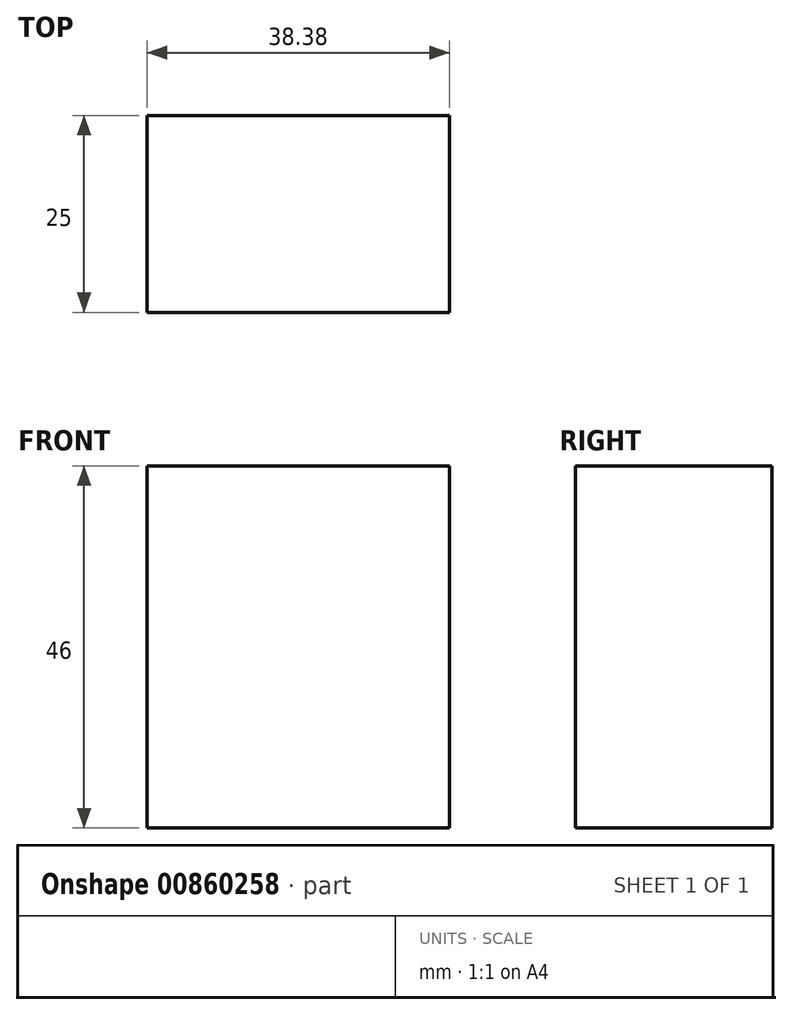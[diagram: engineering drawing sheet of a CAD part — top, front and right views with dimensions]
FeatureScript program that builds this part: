
annotation { "Feature Type Name" : "Feature", "Feature Type Description" : "" }
export const myFeature = defineFeature(function(context is Context, id is Id, definition is map)
    precondition{}
    {
        {
            var Q0;
            Q0=qCreatedBy(makeId("Front.planeOp"),FACE);
            var sketch = newSketch(context, id + "F0", { "sketchPlane" : qUnion([Q0])});
            skLineSegment(sketch, "E0.bottom", {"start": v(-116.32, 40.69) * mm, "end": v(-77.94, 40.69) * mm});
            skLineSegment(sketch, "E0.top", {"start": v(-116.32, -5.3) * mm, "end": v(-77.94, -5.3) * mm});
            skLineSegment(sketch, "E0.left", {"start": v(-116.32, 40.69) * mm, "end": v(-116.32, -5.3) * mm});
            skLineSegment(sketch, "E0.right", {"start": v(-77.94, 40.69) * mm, "end": v(-77.94, -5.3) * mm});
            skSolve(sketch);
        }
        {
            var Q0;
            Q0 = qSketchRegion(id + "F0", true);
            extrude(context, id + "F1", {"entities" : qUnion([Q0]), "depth" : 25 * mm, "offsetDistance" : 25 * mm});
        }
    });
